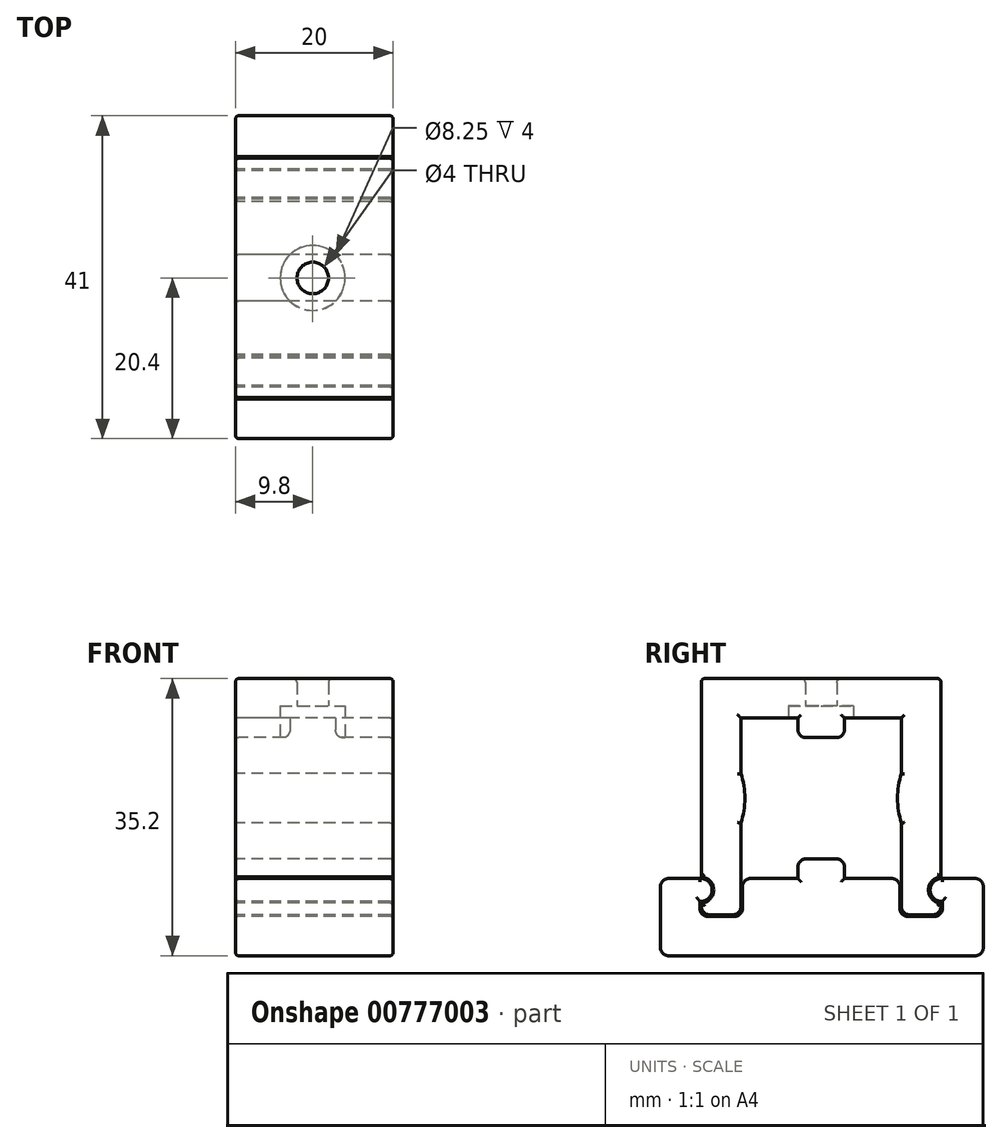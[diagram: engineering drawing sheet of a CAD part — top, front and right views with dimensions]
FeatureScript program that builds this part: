
annotation { "Feature Type Name" : "Feature", "Feature Type Description" : "" }
export const myFeature = defineFeature(function(context is Context, id is Id, definition is map)
    precondition{}
    {
        {
            var Q0;
            Q0=qCreatedBy(makeId("Right.planeOp"),FACE);
            var sketch = newSketch(context, id + "F0", { "sketchPlane" : qUnion([Q0])});
            skLineSegment(sketch, "E0.bottom", {"start": v(10, -10) * mm, "end": v(-10, -10) * mm, "construction": true});
            skLineSegment(sketch, "E0.top", {"start": v(10, 10) * mm, "end": v(-10, 10) * mm, "construction": true});
            skLineSegment(sketch, "E0.left", {"start": v(10, -10) * mm, "end": v(10, 10) * mm, "construction": true});
            skLineSegment(sketch, "E0.right", {"start": v(-10, -10) * mm, "end": v(-10, 10) * mm, "construction": true});
            skPoint(sketch, "E0.middle", {"position": v(0, 0) * mm});
            skLineSegment(sketch, "E1.bottom", {"start": v(-4, 4) * mm, "end": v(4, 4) * mm, "construction": true});
            skLineSegment(sketch, "E1.top", {"start": v(-4, -4) * mm, "end": v(4, -4) * mm, "construction": true});
            skLineSegment(sketch, "E1.left", {"start": v(-4, 4) * mm, "end": v(-4, -4) * mm, "construction": true});
            skLineSegment(sketch, "E1.right", {"start": v(4, 4) * mm, "end": v(4, -4) * mm, "construction": true});
            skLineSegment(sketch, "E2.bottom", {"start": v(3.15, -25) * mm, "end": v(-3.15, -25) * mm, "construction": true});
            skLineSegment(sketch, "E2.top", {"start": v(3.15, 25) * mm, "end": v(-3.15, 25) * mm, "construction": true});
            skLineSegment(sketch, "E2.left", {"start": v(3.15, -25) * mm, "end": v(3.15, 25) * mm, "construction": true});
            skLineSegment(sketch, "E2.right", {"start": v(-3.15, -25) * mm, "end": v(-3.15, 25) * mm, "construction": true});
            skLineSegment(sketch, "E3.bottom", {"start": v(25, -3.15) * mm, "end": v(-25, -3.15) * mm, "construction": true});
            skLineSegment(sketch, "E3.top", {"start": v(25, 3.15) * mm, "end": v(-25, 3.15) * mm, "construction": true});
            skLineSegment(sketch, "E3.left", {"start": v(25, -3.15) * mm, "end": v(25, 3.15) * mm, "construction": true});
            skLineSegment(sketch, "E3.right", {"start": v(-25, -3.15) * mm, "end": v(-25, 3.15) * mm, "construction": true});
            skSolve(sketch);
        }
        {
            assignVariable(context, id + "F1", {"name" : "ArmW", "anyValue" : 20});
        }
        {
            assignVariable(context, id + "F2", {"name" : "NobH", "anyValue" : 2.5});
        }
        {
            var Q0;
            Q0=qCreatedBy(makeId("Right.planeOp"),FACE);
            var sketch = newSketch(context, id + "F3", { "sketchPlane" : qUnion([Q0])});
            skLineSegment(sketch, "E4.bottom", {"start": v(-2.95, 10.2) * mm, "end": v(2.95, 10.2) * mm});
            skLineSegment(sketch, "E4.top", {"start": v(-1.95, 7.7) * mm, "end": v(1.95, 7.7) * mm});
            skLineSegment(sketch, "E4.left", {"start": v(-2.95, 10.2) * mm, "end": v(-2.95, 8.7) * mm});
            skLineSegment(sketch, "E4.right", {"start": v(2.95, 10.2) * mm, "end": v(2.95, 8.7) * mm});
            skLineSegment(sketch, "E5.bottom", {"start": v(-15.2, 15.2) * mm, "end": v(15.2, 15.2) * mm});
            skLineSegment(sketch, "E5.top", {"start": v(-15.2, 10.2) * mm, "end": v(15.2, 10.2) * mm});
            skLineSegment(sketch, "E5.left", {"start": v(-15.2, 15.2) * mm, "end": v(-15.2, 10.2) * mm});
            skLineSegment(sketch, "E5.right", {"start": v(15.2, 15.2) * mm, "end": v(15.2, 10.2) * mm});
            skLineSegment(sketch, "E6.bottom", {"start": v(10.2, 10.2) * mm, "end": v(15.2, 10.2) * mm});
            skLineSegment(sketch, "E6.top", {"start": v(11.2, -14.8) * mm, "end": v(14.2, -14.8) * mm});
            skLineSegment(sketch, "E6.left", {"start": v(10.2, 10.2) * mm, "end": v(10.2, -13.8) * mm});
            skLineSegment(sketch, "E6.right", {"start": v(15.2, -10) * mm, "end": v(15.2, -10.09) * mm});
            skLineSegment(sketch, "E7.bottom", {"start": v(-15.2, 10.2) * mm, "end": v(-10.2, 10.2) * mm});
            skLineSegment(sketch, "E7.top", {"start": v(-14.2, -14.8) * mm, "end": v(-11.2, -14.8) * mm});
            skLineSegment(sketch, "E7.left", {"start": v(-15.2, 10.2) * mm, "end": v(-15.2, -10) * mm});
            skLineSegment(sketch, "E7.right", {"start": v(-10.2, 10.2) * mm, "end": v(-10.2, -13.8) * mm});
            skLineSegment(sketch, "E8.bottom", {"start": v(9.7, -1.7) * mm, "end": v(-9.7, -1.7) * mm, "construction": true});
            skLineSegment(sketch, "E8.top", {"start": v(9.7, 1.7) * mm, "end": v(-9.7, 1.7) * mm, "construction": true});
            skLineSegment(sketch, "E8.left", {"start": v(9.7, -1.7) * mm, "end": v(9.7, 1.7) * mm, "construction": true});
            skLineSegment(sketch, "E8.right", {"start": v(-9.7, -1.7) * mm, "end": v(-9.7, 1.7) * mm, "construction": true});
            skPoint(sketch, "E8.middle", {"position": v(0, 0) * mm});
            skPoint(sketch, "E9", {"position": v(-10.2, 3.15) * mm});
            skPoint(sketch, "E10", {"position": v(-10.2, -3.15) * mm});
            skPoint(sketch, "E11", {"position": v(-9.7, 0) * mm});
            skPoint(sketch, "E12", {"position": v(10.2, 3.15) * mm});
            skPoint(sketch, "E13", {"position": v(10.2, -3.15) * mm});
            skPoint(sketch, "E14", {"position": v(9.7, 0) * mm});
            skArc(sketch, "E15", {"start": v(-10.2, -3.15) * mm, "mid": v(-9.7, 0) * mm, "end": v(-10.2, 3.15) * mm});
            skArc(sketch, "E16", {"start": v(10.2, 3.15) * mm, "mid": v(9.7, 0) * mm, "end": v(10.2, -3.15) * mm});
            skLineSegment(sketch, "E17.bottom", {"start": v(-9, -10.2) * mm, "end": v(9, -10.2) * mm});
            skLineSegment(sketch, "E17.left", {"start": v(-10, -11.2) * mm, "end": v(-10, -14) * mm});
            skLineSegment(sketch, "E17.right", {"start": v(10, -11.2) * mm, "end": v(10, -14) * mm});
            skLineSegment(sketch, "E18.bottom", {"start": v(-19.4, -10.2) * mm, "end": v(-15.4, -10.2) * mm});
            skLineSegment(sketch, "E18.top", {"start": v(-19.4, -20) * mm, "end": v(-15.4, -20) * mm});
            skLineSegment(sketch, "E18.left", {"start": v(-20.4, -11.2) * mm, "end": v(-20.4, -19) * mm});
            skLineSegment(sketch, "E18.right", {"start": v(-15.4, -13.1) * mm, "end": v(-15.4, -14) * mm});
            skLineSegment(sketch, "E19.bottom", {"start": v(15.4, -10.2) * mm, "end": v(19.6, -10.2) * mm});
            skLineSegment(sketch, "E19.top", {"start": v(15.6, -20) * mm, "end": v(19.6, -20) * mm});
            skLineSegment(sketch, "E19.left", {"start": v(15.4, -13.1) * mm, "end": v(15.4, -14) * mm});
            skLineSegment(sketch, "E19.right", {"start": v(20.6, -11.2) * mm, "end": v(20.6, -19) * mm});
            skLineSegment(sketch, "E20.bottom", {"start": v(-14.4, -15) * mm, "end": v(-11, -15) * mm});
            skLineSegment(sketch, "E20.top", {"start": v(-15.4, -20) * mm, "end": v(15.6, -20) * mm});
            skLineSegment(sketch, "E20.left", {"start": v(-15.4, -15) * mm, "end": v(-15.4, -20) * mm});
            skLineSegment(sketch, "E20.right", {"start": v(15.6, -20) * mm, "end": v(15.6, -20) * mm});
            skLineSegment(sketch, "E21.bottom", {"start": v(-1.95, -7.7) * mm, "end": v(1.95, -7.7) * mm});
            skLineSegment(sketch, "E21.top", {"start": v(-2.95, -10.2) * mm, "end": v(2.95, -10.2) * mm});
            skLineSegment(sketch, "E21.left", {"start": v(-2.95, -8.7) * mm, "end": v(-2.95, -10.2) * mm});
            skLineSegment(sketch, "E21.right", {"start": v(2.95, -8.7) * mm, "end": v(2.95, -10.2) * mm});
            skPoint(sketch, "E22", {"position": v(-15.2, -10) * mm});
            skPoint(sketch, "E23", {"position": v(-15.2, -13.3) * mm});
            skPoint(sketch, "E24", {"position": v(-15.4, -13.1) * mm});
            skPoint(sketch, "E25", {"position": v(-13.65, -11.8) * mm});
            skPoint(sketch, "E26", {"position": v(-13.85, -11.8) * mm});
            skArc(sketch, "E27", {"start": v(-15.2, -13.3) * mm, "mid": v(-13.64, -11.65) * mm, "end": v(-15.2, -10) * mm});
            skArc(sketch, "E28", {"start": v(-15.4, -13.1) * mm, "mid": v(-13.84, -11.65) * mm, "end": v(-15.4, -10.2) * mm});
            skLineSegment(sketch, "E29.trimOffspring", {"start": v(-15.2, -13.3) * mm, "end": v(-15.2, -13.8) * mm});
            skPoint(sketch, "E30.MirrorP", {"position": v(15.2, -10) * mm});
            skArc(sketch, "E31.MirrorCS", {"start": v(15.2, -13.3) * mm, "mid": v(13.64, -11.65) * mm, "end": v(15.2, -10) * mm});
            skArc(sketch, "E32.MirrorCS", {"start": v(15.4, -13.1) * mm, "mid": v(13.84, -11.65) * mm, "end": v(15.4, -10.2) * mm});
            skPoint(sketch, "E33.MirrorP", {"position": v(13.85, -11.8) * mm});
            skPoint(sketch, "E34.MirrorP", {"position": v(13.65, -11.8) * mm});
            skPoint(sketch, "E35.MirrorP", {"position": v(15.4, -13.1) * mm});
            skPoint(sketch, "E36.MirrorP", {"position": v(15.2, -13.3) * mm});
            skLineSegment(sketch, "E37.trimOffspring", {"start": v(15.2, -13.3) * mm, "end": v(15.2, -13.8) * mm});
            skPoint(sketch, "E38.visualSharp", {"position": v(-15.2, 15.2) * mm});
            skPoint(sketch, "E39.visualSharp", {"position": v(-20.4, -10.2) * mm});
            skArc(sketch, "E39.filletArc", {"start": v(-19.4, -10.2) * mm, "mid": v(-20.1, -10.5) * mm, "end": v(-20.4, -11.2) * mm});
            skPoint(sketch, "E40.visualSharp", {"position": v(-20.4, -20) * mm});
            skArc(sketch, "E40.filletArc", {"start": v(-20.4, -19) * mm, "mid": v(-20.1, -19.7) * mm, "end": v(-19.4, -20) * mm});
            skPoint(sketch, "E41.visualSharp", {"position": v(20.6, -20) * mm});
            skArc(sketch, "E41.filletArc", {"start": v(19.6, -20) * mm, "mid": v(20.3, -19.7) * mm, "end": v(20.6, -19) * mm});
            skPoint(sketch, "E42.visualSharp", {"position": v(20.6, -10.2) * mm});
            skArc(sketch, "E42.filletArc", {"start": v(20.6, -11.2) * mm, "mid": v(20.3, -10.5) * mm, "end": v(19.6, -10.2) * mm});
            skPoint(sketch, "E43.visualSharp", {"position": v(-2.95, -7.7) * mm});
            skArc(sketch, "E43.filletArc", {"start": v(-1.95, -7.7) * mm, "mid": v(-2.66, -8) * mm, "end": v(-2.95, -8.7) * mm});
            skPoint(sketch, "E44.visualSharp", {"position": v(2.95, -7.7) * mm});
            skArc(sketch, "E44.filletArc", {"start": v(2.95, -8.7) * mm, "mid": v(2.66, -8) * mm, "end": v(1.95, -7.7) * mm});
            skPoint(sketch, "E45.visualSharp", {"position": v(-2.95, 7.7) * mm});
            skArc(sketch, "E45.filletArc", {"start": v(-2.95, 8.7) * mm, "mid": v(-2.66, 8) * mm, "end": v(-1.95, 7.7) * mm});
            skPoint(sketch, "E46.visualSharp", {"position": v(2.95, 7.7) * mm});
            skArc(sketch, "E46.filletArc", {"start": v(1.95, 7.7) * mm, "mid": v(2.66, 8) * mm, "end": v(2.95, 8.7) * mm});
            skPoint(sketch, "E47.visualSharp", {"position": v(10.2, -14.8) * mm});
            skArc(sketch, "E47.filletArc", {"start": v(10.2, -13.8) * mm, "mid": v(10.5, -14.5) * mm, "end": v(11.2, -14.8) * mm});
            skPoint(sketch, "E48.visualSharp", {"position": v(15.2, -14.8) * mm});
            skArc(sketch, "E48.filletArc", {"start": v(14.2, -14.8) * mm, "mid": v(14.9, -14.5) * mm, "end": v(15.2, -13.8) * mm});
            skPoint(sketch, "E49.visualSharp", {"position": v(-10, -10.2) * mm});
            skArc(sketch, "E49.filletArc", {"start": v(-9, -10.2) * mm, "mid": v(-9.7, -10.5) * mm, "end": v(-10, -11.2) * mm});
            skPoint(sketch, "E50.visualSharp", {"position": v(10, -10.2) * mm});
            skArc(sketch, "E50.filletArc", {"start": v(10, -11.2) * mm, "mid": v(9.7, -10.5) * mm, "end": v(9, -10.2) * mm});
            skPoint(sketch, "E51.visualSharp", {"position": v(-10.2, -14.8) * mm});
            skArc(sketch, "E51.filletArc", {"start": v(-11.2, -14.8) * mm, "mid": v(-10.5, -14.5) * mm, "end": v(-10.2, -13.8) * mm});
            skPoint(sketch, "E52.visualSharp", {"position": v(-15.2, -14.8) * mm});
            skArc(sketch, "E52.filletArc", {"start": v(-15.2, -13.8) * mm, "mid": v(-14.9, -14.5) * mm, "end": v(-14.2, -14.8) * mm});
            skArc(sketch, "E53.filletArc", {"start": v(-15.4, -14) * mm, "mid": v(-15.1, -14.7) * mm, "end": v(-14.4, -15) * mm});
            skArc(sketch, "E54.filletArc", {"start": v(14.4, -15) * mm, "mid": v(15.1, -14.7) * mm, "end": v(15.4, -14) * mm});
            skLineSegment(sketch, "E55.trimOffspring", {"start": v(11, -15) * mm, "end": v(14.4, -15) * mm});
            skPoint(sketch, "E56.visualSharp", {"position": v(-10, -15) * mm});
            skArc(sketch, "E56.filletArc", {"start": v(-11, -15) * mm, "mid": v(-10.3, -14.7) * mm, "end": v(-10, -14) * mm});
            skPoint(sketch, "E57.visualSharp", {"position": v(10, -15) * mm});
            skArc(sketch, "E57.filletArc", {"start": v(10, -14) * mm, "mid": v(10.3, -14.7) * mm, "end": v(11, -15) * mm});
            skPoint(sketch, "E58.visualSharp", {"position": v(-15.4, -10.2) * mm});
            skLineSegment(sketch, "E59", {"start": v(15.2, 10.2) * mm, "end": v(15.2, -10.09) * mm});
            skSolve(sketch);
        }
        {
            var Q0;
            Q0=qSketchRegion(id+"F3",true);
            extrude(context, id + "F4", {"entities" : qUnion([Q0]), "depth" : (getVariable(context, 'ArmW')) * mm, "offsetDistance" : 25 * mm});
        }
        {
            var Q0;
            Q0=makeQuery(id+"F4.opExtrude","CAP_FACE",FACE,{"disambiguationData":[OSD([sQuery(id+"F3.wireOp",EDGE,"E4.top"),sQuery(id+"F3.wireOp",EDGE,"E4.left"),sQuery(id+"F3.wireOp",EDGE,"E4.right"),sQuery(id+"F3.wireOp",EDGE,"E5.top"),sQuery(id+"F3.wireOp",EDGE,"E5.left"),sQuery(id+"F3.wireOp",EDGE,"E6.top"),sQuery(id+"F3.wireOp",EDGE,"E6.left"),sQuery(id+"F3.wireOp",EDGE,"E6.right"),sQuery(id+"F3.wireOp",EDGE,"E7.top"),sQuery(id+"F3.wireOp",EDGE,"E7.left"),sQuery(id+"F3.wireOp",EDGE,"E7.right"),sQuery(id+"F3.wireOp",EDGE,"E15"),sQuery(id+"F3.wireOp",EDGE,"E16"),sQuery(id+"F3.wireOp",EDGE,"E27"),sQuery(id+"F3.wireOp",EDGE,"E29.trimOffspring"),sQuery(id+"F3.wireOp",EDGE,"E31.MirrorCS"),sQuery(id+"F3.wireOp",EDGE,"E37.trimOffspring"),sQuery(id+"F3.wireOp",EDGE,"CPXm2P8D-MYPe-24e7-BYdm-IAWXcMyXt9ET"),sQuery(id+"F3.wireOp",EDGE,"Zd5Pprwu-u2Gz-A4pV-qktT-EqDlDXvuVTjz"),sQuery(id+"F3.wireOp",EDGE,"Yqs1rK9N-u7IJ-Y097-vMOV-WPaym0EBePmP"),sQuery(id+"F3.wireOp",EDGE,"nV0X0nJd-f3eA-iQEM-rXcq-amLtK6TaMd1z"),sQuery(id+"F3.wireOp",EDGE,"3807ad3b-ab58-43f6-95fe-ed81e5da2370.filletArc"),sQuery(id+"F3.wireOp",EDGE,"E38.filletArc")])],"isStart":true});
            var Q1;
            Q1=makeQuery(id+"F4.opExtrude","CAP_FACE",FACE,{"disambiguationData":[OSD([sQuery(id+"F3.wireOp",EDGE,"E4.top"),sQuery(id+"F3.wireOp",EDGE,"E4.left"),sQuery(id+"F3.wireOp",EDGE,"E4.right"),sQuery(id+"F3.wireOp",EDGE,"E5.top"),sQuery(id+"F3.wireOp",EDGE,"E5.left"),sQuery(id+"F3.wireOp",EDGE,"E6.top"),sQuery(id+"F3.wireOp",EDGE,"E6.left"),sQuery(id+"F3.wireOp",EDGE,"E6.right"),sQuery(id+"F3.wireOp",EDGE,"E7.top"),sQuery(id+"F3.wireOp",EDGE,"E7.left"),sQuery(id+"F3.wireOp",EDGE,"E7.right"),sQuery(id+"F3.wireOp",EDGE,"E15"),sQuery(id+"F3.wireOp",EDGE,"E16"),sQuery(id+"F3.wireOp",EDGE,"E27"),sQuery(id+"F3.wireOp",EDGE,"E29.trimOffspring"),sQuery(id+"F3.wireOp",EDGE,"E31.MirrorCS"),sQuery(id+"F3.wireOp",EDGE,"E37.trimOffspring"),sQuery(id+"F3.wireOp",EDGE,"CPXm2P8D-MYPe-24e7-BYdm-IAWXcMyXt9ET"),sQuery(id+"F3.wireOp",EDGE,"Zd5Pprwu-u2Gz-A4pV-qktT-EqDlDXvuVTjz"),sQuery(id+"F3.wireOp",EDGE,"Yqs1rK9N-u7IJ-Y097-vMOV-WPaym0EBePmP"),sQuery(id+"F3.wireOp",EDGE,"nV0X0nJd-f3eA-iQEM-rXcq-amLtK6TaMd1z"),sQuery(id+"F3.wireOp",EDGE,"3807ad3b-ab58-43f6-95fe-ed81e5da2370.filletArc"),sQuery(id+"F3.wireOp",EDGE,"E38.filletArc")])],"isStart":false});
            var Q2;
            Q2=makeQuery(id+"F4.opExtrude","SWEPT_EDGE",EDGE,{"disambiguationData":[OSD([sQuery(id+"F3.wireOp",EDGE,"E5.bottom"),sQuery(id+"F3.wireOp",EDGE,"E5.left")])]});
            var Q3;
            Q3=makeQuery(id+"F4.opExtrude","SWEPT_EDGE",EDGE,{"disambiguationData":[OSD([sQuery(id+"F3.wireOp",EDGE,"E5.bottom"),sQuery(id+"F3.wireOp",EDGE,"E5.right")])]});
            fillet(context, id + "F5", {"entities" : qUnion([Q0, Q1, Q2, Q3]), "radius" : .4 * mm, "tangentPropagation" : true, "allowEdgeOverflow" : false});
        }
        {
            var Q0;
            Q0=makeQuery(id+"F4.opExtrude","CAP_FACE",FACE,{"disambiguationData":[OSD([sQuery(id+"F3.wireOp",EDGE,"E17.bottom"),sQuery(id+"F3.wireOp",EDGE,"E17.left"),sQuery(id+"F3.wireOp",EDGE,"E17.right"),sQuery(id+"F3.wireOp",EDGE,"E18.bottom"),sQuery(id+"F3.wireOp",EDGE,"E18.top"),sQuery(id+"F3.wireOp",EDGE,"E18.left"),sQuery(id+"F3.wireOp",EDGE,"E18.right"),sQuery(id+"F3.wireOp",EDGE,"E19.bottom"),sQuery(id+"F3.wireOp",EDGE,"E19.top"),sQuery(id+"F3.wireOp",EDGE,"E19.left"),sQuery(id+"F3.wireOp",EDGE,"E19.right"),sQuery(id+"F3.wireOp",EDGE,"E20.bottom"),sQuery(id+"F3.wireOp",EDGE,"E20.top"),sQuery(id+"F3.wireOp",EDGE,"E21.bottom"),sQuery(id+"F3.wireOp",EDGE,"E21.left"),sQuery(id+"F3.wireOp",EDGE,"E21.right"),sQuery(id+"F3.wireOp",EDGE,"E28"),sQuery(id+"F3.wireOp",EDGE,"E32.MirrorCS")])],"isStart":false});
            var Q1;
            Q1=makeQuery(id+"F4.opExtrude","CAP_FACE",FACE,{"disambiguationData":[OSD([sQuery(id+"F3.wireOp",EDGE,"E17.bottom"),sQuery(id+"F3.wireOp",EDGE,"E17.left"),sQuery(id+"F3.wireOp",EDGE,"E17.right"),sQuery(id+"F3.wireOp",EDGE,"E18.bottom"),sQuery(id+"F3.wireOp",EDGE,"E18.top"),sQuery(id+"F3.wireOp",EDGE,"E18.left"),sQuery(id+"F3.wireOp",EDGE,"E18.right"),sQuery(id+"F3.wireOp",EDGE,"E19.bottom"),sQuery(id+"F3.wireOp",EDGE,"E19.top"),sQuery(id+"F3.wireOp",EDGE,"E19.left"),sQuery(id+"F3.wireOp",EDGE,"E19.right"),sQuery(id+"F3.wireOp",EDGE,"E20.bottom"),sQuery(id+"F3.wireOp",EDGE,"E20.top"),sQuery(id+"F3.wireOp",EDGE,"E21.bottom"),sQuery(id+"F3.wireOp",EDGE,"E21.left"),sQuery(id+"F3.wireOp",EDGE,"E21.right"),sQuery(id+"F3.wireOp",EDGE,"E28"),sQuery(id+"F3.wireOp",EDGE,"E32.MirrorCS")])],"isStart":true});
            fillet(context, id + "F6", {"entities" : qUnion([Q0, Q1]), "radius" : .4 * mm, "allowEdgeOverflow" : false});
        }
        {
            var Q0;
            Q0=makeQuery(id+"F4.opExtrude","SWEPT_FACE",FACE,{"disambiguationData":[OSD([sQuery(id+"F3.wireOp",EDGE,"E4.top")])]});
            cPlane(context, id + "F7", {"entities" : qUnion([Q0]), "cplaneType" : CPlaneType.OFFSET, "offset" : 0 * mm, "width" : 150 * mm, "height" : 150 * mm});
        }
        {
            var Q0;
            Q0=qCreatedBy(id+"F7.planeOp",FACE);
            var sketch = newSketch(context, id + "F8", { "sketchPlane" : qUnion([Q0])});
            skPoint(sketch, "E60.0", {"position": v(0, -15.2) * mm});
            skPoint(sketch, "E61.0", {"position": v(0, 15.2) * mm});
            skPoint(sketch, "E62.0", {"position": v(19.6, 15.2) * mm});
            skPoint(sketch, "E63.0", {"position": v(19.6, -15.2) * mm});
            skLineSegment(sketch, "E64", {"start": v(19.6, 15.2) * mm, "end": v(19.6, -15.2) * mm, "construction": true});
            skLineSegment(sketch, "E65", {"start": v(19.6, -15.2) * mm, "end": v(0, 15.2) * mm, "construction": true});
            skLineSegment(sketch, "E66", {"start": v(19.6, 15.2) * mm, "end": v(0, -15.2) * mm, "construction": true});
            skLineSegment(sketch, "E67", {"start": v(0, 15.2) * mm, "end": v(19.6, 15.2) * mm, "construction": true});
            skLineSegment(sketch, "E68", {"start": v(0, -15.2) * mm, "end": v(19.6, -15.2) * mm, "construction": true});
            skPoint(sketch, "E69", {"position": v(9.8, 15.2) * mm});
            skPoint(sketch, "E70", {"position": v(9.8, 0) * mm});
            skSolve(sketch);
        }
        {
            var Q0;
            Q0=sQuery(id+"F8.wireOp",VERTEX,"E70");
            var Q1;
            Q1=makeQuery(id+"F4.opExtrude","SWEPT_BODY",BODY,{"disambiguationData":[OSD([sQuery(id+"F3.wireOp",EDGE,"E4.top"),sQuery(id+"F3.wireOp",EDGE,"E4.left"),sQuery(id+"F3.wireOp",EDGE,"E4.right"),sQuery(id+"F3.wireOp",EDGE,"E5.bottom"),sQuery(id+"F3.wireOp",EDGE,"E5.top"),sQuery(id+"F3.wireOp",EDGE,"E5.left"),sQuery(id+"F3.wireOp",EDGE,"E5.right"),sQuery(id+"F3.wireOp",EDGE,"E6.top"),sQuery(id+"F3.wireOp",EDGE,"E6.left"),sQuery(id+"F3.wireOp",EDGE,"E6.right"),sQuery(id+"F3.wireOp",EDGE,"E7.top"),sQuery(id+"F3.wireOp",EDGE,"E7.left"),sQuery(id+"F3.wireOp",EDGE,"E7.right"),sQuery(id+"F3.wireOp",EDGE,"E15"),sQuery(id+"F3.wireOp",EDGE,"E16"),sQuery(id+"F3.wireOp",EDGE,"E27"),sQuery(id+"F3.wireOp",EDGE,"E29.trimOffspring"),sQuery(id+"F3.wireOp",EDGE,"E31.MirrorCS"),sQuery(id+"F3.wireOp",EDGE,"E37.trimOffspring"),sQuery(id+"F3.wireOp",EDGE,"E45.filletArc"),sQuery(id+"F3.wireOp",EDGE,"E46.filletArc"),sQuery(id+"F3.wireOp",EDGE,"E47.filletArc"),sQuery(id+"F3.wireOp",EDGE,"E48.filletArc"),sQuery(id+"F3.wireOp",EDGE,"E51.filletArc"),sQuery(id+"F3.wireOp",EDGE,"E52.filletArc"),sQuery(id+"F3.wireOp",EDGE,"E59")])]});
            hole(context, id + "F9", {"style" : HoleStyle.C_BORE, "endStyle" : HoleEndStyle.THROUGH, "holeDiameter" : 4 * mm, "cBoreDiameter" : 8.25 * mm, "cBoreDepth" : (getVariable(context, 'NobH') + 1.5) * mm, "majorDiameter" : 3 * mm, "isTappedThrough" : true, "tappedDepth" : 6.5 * mm, "tapClearance" : 3, "startFromSketch" : true, "locations" : qUnion([Q0]), "scope" : qUnion([Q1])});
        }
        {
            var Q0;
            Q0=makeQuery(id+"F4.opExtrude","SWEPT_FACE",FACE,{"disambiguationData":[OSD([sQuery(id+"F3.wireOp",EDGE,"E5.bottom")])]});
            fillet(context, id + "F10", {"entities" : qUnion([Q0]), "radius" : .5 * mm, "tangentPropagation" : true, "allowEdgeOverflow" : false});
        }
    });
